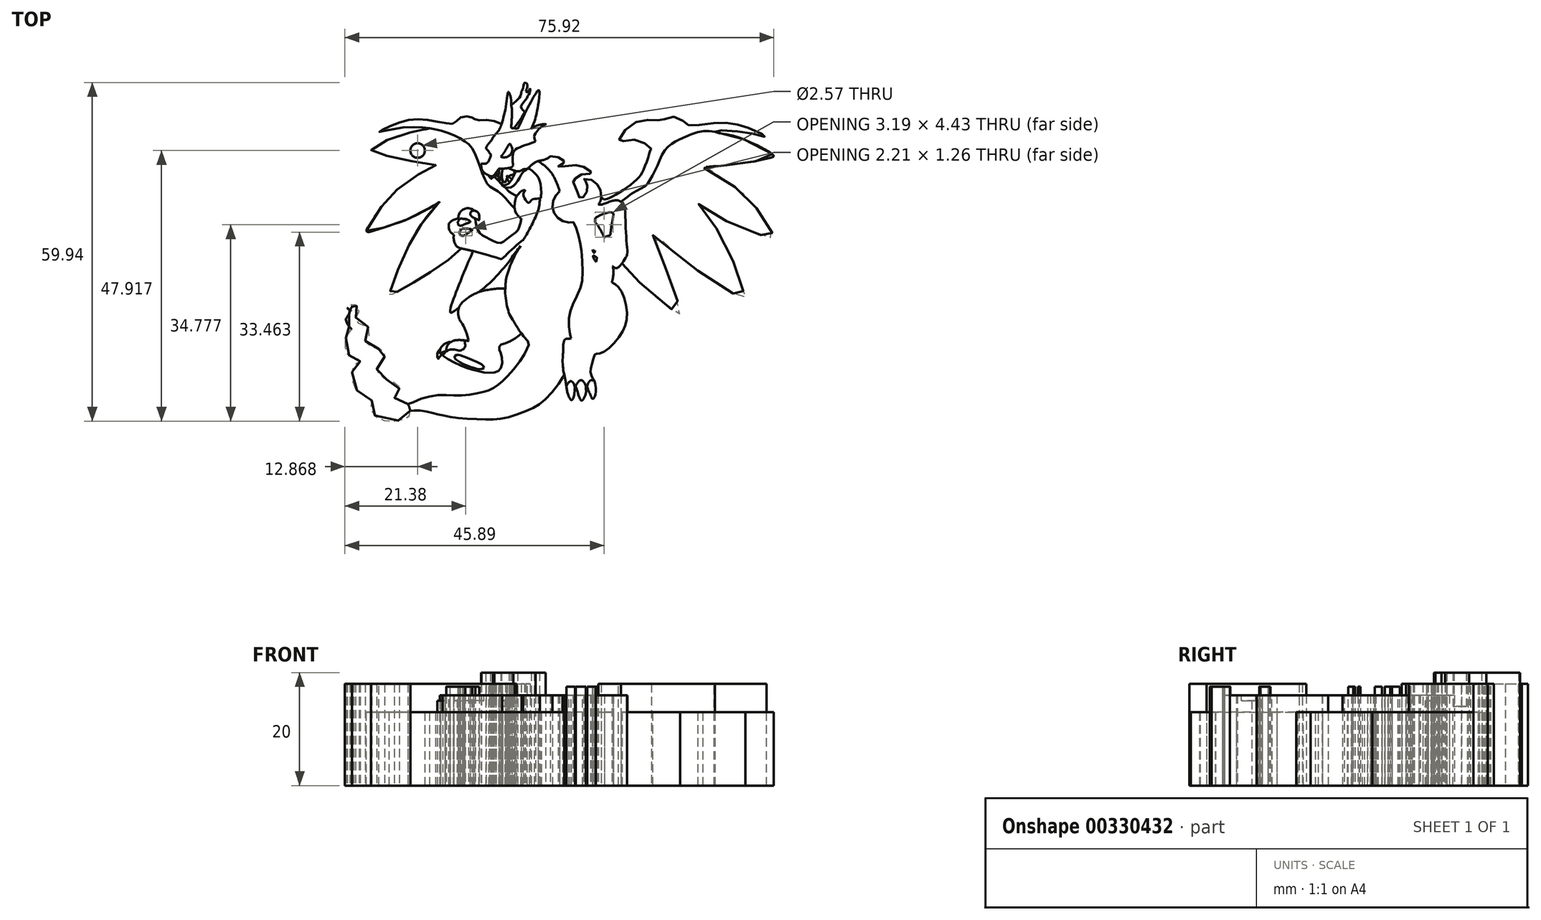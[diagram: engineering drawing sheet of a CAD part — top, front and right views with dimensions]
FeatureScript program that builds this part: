
annotation { "Feature Type Name" : "Feature", "Feature Type Description" : "" }
export const myFeature = defineFeature(function(context is Context, id is Id, definition is map)
    precondition{}
    {
        {
            var Q0;
            Q0=qCreatedBy(makeId("Top.planeOp"),FACE);
            var sketch = newSketch(context, id + "F0", { "sketchPlane" : qUnion([Q0])});
            skFitSpline(sketch, "E0", {"points": [v(-5.28, 21.77) * mm, v(-4.35, 23.75) * mm, v(-3.93, 25.14) * mm, v(-3.6, 26.95) * mm, v(-3.43, 29.56) * mm, v(-7.38, 22.36) * mm], "startDerivative": vector(5.95, 11.84) * mm, "endDerivative": vector(-15.93, -33.46) * mm});
            skFitSpline(sketch, "E1", {"points": [v(-13.6, 15.69) * mm, v(-13.11, 14.98) * mm, v(-12.33, 14.52) * mm, v(-11.58, 14.4) * mm, v(-10.53, 15.69) * mm, v(-10.29, 15.69) * mm, v(-8.86, 15.81) * mm, v(-8.3, 15.96) * mm, v(-7.97, 16.3) * mm], "startDerivative": vector(3.2, -6) * mm, "endDerivative": vector(3.22, 4.12) * mm});
            skFitSpline(sketch, "E2", {"points": [v(-7.97, 16.3) * mm, v(-8.08, 16.94) * mm, v(-8.08, 17.85) * mm, v(-7.65, 19.02) * mm, v(-4.05, 20.54) * mm, v(-3.37, 21.36) * mm, v(-2.92, 22.7) * mm, v(0.36, 24.41) * mm, v(1.08, 25) * mm, v(1.01, 25.22) * mm, v(0.6, 25.6) * mm, v(4.78, 27.86) * mm, v(5.06, 28.34) * mm, v(5.67, 28.87) * mm, v(6.78, 30.14) * mm, v(7.14, 30.28) * mm, v(7.3, 30.62) * mm, v(7.32, 30.06) * mm, v(6.76, 29.65) * mm, v(6.72, 29.1) * mm, v(6.58, 28.8) * mm, v(6.39, 28.52) * mm, v(6.25, 28.42) * mm, v(6.13, 28.24) * mm, v(6.03, 28.04) * mm, v(6, 27.9) * mm, v(6.19, 27.88) * mm, v(6.4, 28.02) * mm, v(6.72, 28.24) * mm, v(6.88, 28.28) * mm, v(6.88, 28.16) * mm, v(6.7, 27.82) * mm, v(5.89, 27.13) * mm, v(5.65, 26.9) * mm, v(5.2, 26.53) * mm, v(4.84, 26.26) * mm, v(3.81, 25.68) * mm, v(3.71, 24.24) * mm, v(3.7, 24.22) * mm, v(2.8, 23.29) * mm, v(0.4, 21.79) * mm, v(-0.37, 20.97) * mm, v(-0.98, 18.57) * mm, v(-2.38, 17.33) * mm, v(-4.18, 16.8) * mm, v(-5.54, 15.69) * mm, v(-6.16, 15.61) * mm, v(-6.94, 15.24) * mm, v(-8.86, 15.81) * mm], "startDerivative": vector(-6.92, 33.48) * mm, "endDerivative": vector(-66.57, 30.7) * mm});
            skFitSpline(sketch, "E3", {"points": [v(-13.68, 16.59) * mm, v(-13.88, 16.97) * mm, v(-13.91, 17.58) * mm, v(-13.68, 18.49) * mm, v(-12.75, 19.2) * mm], "startDerivative": vector(-1.25, 1.88) * mm, "endDerivative": vector(3.52, 2.03) * mm});
            skFitSpline(sketch, "E4", {"points": [v(-7.84, 22.85) * mm, v(-6.1, 25.41) * mm, v(-6.05, 25.88) * mm, v(-6.4, 26.2) * mm, v(-6.58, 26.84) * mm, v(-5.75, 27.92) * mm, v(-5.4, 28.63) * mm, v(-5.03, 29.25) * mm, v(-4.96, 29.82) * mm, v(-5.02, 29.88) * mm, v(-5.28, 29.43) * mm, v(-5.6, 29.25) * mm, v(-5.72, 29.44) * mm], "startDerivative": vector(12.32, 16.66) * mm, "endDerivative": vector(-1.84, 5.18) * mm});
            skFitSpline(sketch, "E5", {"points": [v(-8.36, 26.94) * mm, v(-6.68, 28.63) * mm, v(-6.54, 29.36) * mm, v(-6.31, 29.73) * mm, v(-6, 30.9) * mm, v(-5.6, 30.79) * mm, v(-5.48, 30.17) * mm, v(-5.68, 29.67) * mm, v(-5.72, 29.44) * mm], "startDerivative": vector(12.02, 9.65) * mm, "endDerivative": vector(-0.19, -3.77) * mm});
            skFitSpline(sketch, "E6", {"points": [v(-18.52, 3.96) * mm, v(-18.52, 3.16) * mm, v(-18.03, 1.98) * mm, v(-16.6, 1.46) * mm, v(-10.77, -0.1) * mm, v(-10.08, -0.26) * mm, v(-8.86, 0.8) * mm, v(-6.22, 3.05) * mm, v(-7.4, 0.84) * mm, v(-9.32, -4.35) * mm, v(-9.39, -5.44) * mm, v(-9.9, -5.49) * mm, v(-13.17, -5.89) * mm, v(-15.75, -6.98) * mm, v(-17.55, -8.73) * mm, v(-17.7, -10.16) * mm, v(-17.38, -11.25) * mm, v(-16.9, -11.96) * mm, v(-15.92, -14.74) * mm, v(-16.19, -14.77) * mm, v(-18.52, -14.74) * mm, v(-19.2, -15.08) * mm, v(-19.2, -15) * mm, v(-20.22, -15.37) * mm, v(-20.76, -15.95) * mm, v(-20.99, -16.28) * mm, v(-21.34, -16.8) * mm, v(-21.38, -17.79) * mm, v(-21.22, -17.93) * mm, v(-21.1, -17.72) * mm, v(-20.5, -17.23) * mm, v(-20.41, -17.34) * mm, v(-18.45, -18.61) * mm, v(-15.46, -19.8) * mm, v(-12.83, -20.4) * mm, v(-10.93, -20.29) * mm, v(-10.08, -19.37) * mm, v(-10.08, -17.3) * mm, v(-10.48, -16.23) * mm, v(-10.3, -15.57) * mm, v(-9.43, -15.22) * mm, v(-7.19, -14.06) * mm, v(-6.5, -13.48) * mm, v(-6.42, -13.68) * mm, v(-5.24, -15.05) * mm, v(-5.35, -15.8) * mm, v(-6.3, -17.62) * mm, v(-9.2, -21.27) * mm, v(-10.67, -22.6) * mm, v(-12.14, -23.46) * mm, v(-13.8, -23.94) * mm, v(-16.9, -24.43) * mm, v(-20.14, -24.36) * mm, v(-24.01, -24.93) * mm, v(-26.62, -25.94) * mm, v(-26.97, -25.8) * mm, v(-28.86, -25.04) * mm, v(-29.03, -24.8) * mm, v(-29.01, -24.57) * mm, v(-28.4, -23.96) * mm, v(-28.17, -23.14) * mm, v(-28.53, -22.45) * mm, v(-30.2, -21.74) * mm, v(-31.45, -20.92) * mm, v(-32.1, -20.01) * mm, v(-31.97, -19.38) * mm, v(-30.88, -18.04) * mm, v(-30.73, -17.39) * mm, v(-30.82, -16.86) * mm, v(-31.45, -16.3) * mm, v(-32.08, -16.17) * mm, v(-34.01, -15.35) * mm, v(-34.14, -14.66) * mm, v(-33.4, -13.56) * mm, v(-33.66, -12.37) * mm, v(-35.57, -11.55) * mm, v(-35.88, -10.75) * mm, v(-35.4, -10.01) * mm, v(-35.36, -9.13) * mm, v(-36.1, -8.37) * mm, v(-36.87, -8.29) * mm, v(-36.51, -8.52) * mm, v(-36.58, -8.69) * mm, v(-36.24, -9.05) * mm, v(-36.3, -9.42) * mm, v(-36.47, -9.57) * mm, v(-36.83, -9.09) * mm, v(-37.35, -8.98) * mm, v(-37.16, -9.17) * mm, v(-36.93, -9.6) * mm, v(-37.45, -10.61) * mm, v(-37.6, -11.13) * mm, v(-36.98, -12.33) * mm, v(-36.63, -12.74) * mm, v(-37.36, -13.61) * mm, v(-37.78, -15.51) * mm, v(-37.33, -17.11) * mm, v(-35.93, -17.85) * mm, v(-35.53, -17.9) * mm, v(-35.08, -18.41) * mm, v(-35.81, -18.85) * mm, v(-36.49, -19.88) * mm, v(-36.43, -21.68) * mm, v(-35.7, -23.48) * mm, v(-33.32, -24.94) * mm, v(-33.06, -25.2) * mm, v(-33.16, -26.3) * mm, v(-32.83, -27.52) * mm, v(-31.17, -28.81) * mm, v(-27.42, -28.69) * mm, v(-26.3, -27.93) * mm, v(-26.27, -26.94) * mm, v(-26.6, -25.97) * mm], "startDerivative": vector(-9.43, -93.41) * mm, "endDerivative": vector(-46.86, 115.32) * mm});
            skFitSpline(sketch, "E7", {"points": [v(-26.22, -27.2) * mm, v(-24.98, -27.1) * mm, v(-22.6, -27.46) * mm, v(-20.73, -27.93) * mm, v(-17.76, -28.4) * mm, v(-12.76, -28.7) * mm, v(-9.46, -28.44) * mm, v(-5, -26.86) * mm, v(-2.21, -25.04) * mm, v(0.9, -20.98) * mm, v(1.03, -20.68) * mm, v(1.41, -22.76) * mm, v(1.62, -23.95) * mm, v(2.3, -25.26) * mm, v(2.75, -24.57) * mm, v(2.96, -23.12) * mm, v(3.1, -22.97) * mm, v(3.43, -23.95) * mm, v(4.03, -25.29) * mm, v(4.26, -25.29) * mm, v(4.89, -23.9) * mm, v(4.92, -23) * mm, v(5.13, -23) * mm, v(5.28, -23.46) * mm, v(5.79, -24.57) * mm, v(6.08, -25.04) * mm, v(6.59, -24.16) * mm, v(6.35, -21.82) * mm, v(6.02, -21.3) * mm, v(5.7, -20.3) * mm, v(5.93, -19.03) * mm, v(6.54, -17.08) * mm, v(6.85, -17.07) * mm, v(8.28, -16.6) * mm, v(11.15, -13.47) * mm, v(12.15, -10.13) * mm, v(11.12, -5.93) * mm, v(9.82, -4.6) * mm, v(8.78, -4.2) * mm, v(7.78, -4.26) * mm], "startDerivative": vector(49.4, 7.29) * mm, "endDerivative": vector(-49.28, -7.9) * mm});
            skFitSpline(sketch, "E8", {"points": [v(9.47, -4.4) * mm, v(9.6, -3.94) * mm, v(9.59, -1.55) * mm, v(9.09, -0.86) * mm, v(9.84, -0.18) * mm, v(9.93, -0.58) * mm], "startDerivative": vector(0.87, 2.22) * mm, "endDerivative": vector(-0.3, -4.39) * mm});
            skFitSpline(sketch, "E9", {"points": [v(9.09, -0.86) * mm, v(8.73, -1.05) * mm, v(8.28, -1.45) * mm, v(7.43, -1.52) * mm, v(6.75, -0.86) * mm, v(6.18, 0) * mm, v(6.26, 0.34) * mm, v(6.82, 0) * mm, v(6.99, 0.32) * mm, v(7.62, 0.44) * mm, v(8.02, 1.4) * mm, v(7.84, 1.71) * mm, v(6.94, 1.14) * mm, v(5.95, 1.5) * mm, v(6.42, 2.81) * mm, v(9.09, 3.9) * mm, v(9.27, 4.38) * mm, v(9.73, 7.37) * mm, v(9.73, 7.79) * mm, v(9.35, 7.99) * mm, v(8.22, 7.79) * mm, v(6.57, 6.9) * mm, v(6.51, 6.18) * mm, v(5.36, 5.35) * mm], "startDerivative": vector(-12.67, -5.04) * mm, "endDerivative": vector(-28.77, -14.22) * mm});
            skFitSpline(sketch, "E10", {"points": [v(6.51, 6.18) * mm, v(7.06, 5.53) * mm, v(8.14, 3.56) * mm], "startDerivative": vector(1.37, -1.44) * mm, "endDerivative": vector(1.84, -3.64) * mm});
            skFitSpline(sketch, "E11", {"points": [v(9.59, -1.55) * mm, v(9.97, -1.83) * mm, v(10.53, -1.82) * mm, v(11.52, -0.69) * mm, v(12.14, 0.37) * mm, v(12.15, 1.95) * mm, v(11.89, 6.52) * mm, v(11.73, 8.76) * mm, v(11.1, 9.85) * mm, v(9.59, 10.03) * mm, v(7.55, 9.33) * mm, v(6.51, 9.73) * mm], "startDerivative": vector(6.81, -6.46) * mm, "endDerivative": vector(-12.01, 8.1) * mm});
            skFitSpline(sketch, "E12", {"points": [v(7.1, 9.4) * mm, v(7.47, 10.03) * mm, v(7.59, 11.2) * mm, v(7.35, 12.23) * mm, v(6.67, 13.14) * mm, v(5.54, 13.83) * mm, v(4.47, 13.8) * mm, v(4.55, 13.64) * mm, v(4.8, 13.58) * mm, v(5.07, 13.1) * mm, v(5.1, 12.27) * mm, v(4.93, 11.35) * mm, v(4.31, 10.6) * mm, v(4, 10.64) * mm, v(3.62, 10.64) * mm, v(3.52, 11.04) * mm, v(2.6, 13.52) * mm, v(2.75, 13.75) * mm, v(3.34, 14.23) * mm, v(4.77, 14.83) * mm, v(5.95, 14.83) * mm, v(5.74, 15.2) * mm, v(4.31, 16.11) * mm, v(2.7, 16.33) * mm, v(0.2, 16.04) * mm, v(0, 16.1) * mm, v(0.7, 16.57) * mm, v(1.18, 16.79) * mm, v(0.94, 17.15) * mm, v(0, 17.72) * mm, v(-1.4, 17.94) * mm], "startDerivative": vector(13.3, 18.15) * mm, "endDerivative": vector(-34.01, 2.55) * mm});
            skFitSpline(sketch, "E13", {"points": [v(7.58, 10.65) * mm, v(8.05, 10.28) * mm, v(8.35, 10.28) * mm, v(9.37, 10.7) * mm, v(11.83, 12.15) * mm, v(14.05, 13.94) * mm, v(14.85, 15.05) * mm, v(15.92, 17.75) * mm, v(16.46, 19.2) * mm, v(16.82, 18.26) * mm], "startDerivative": vector(6.95, -6.7) * mm, "endDerivative": vector(3.86, -15.3) * mm});
            skFitSpline(sketch, "E14", {"points": [v(16.46, 19.2) * mm, v(15.75, 19.97) * mm, v(13.94, 20.68) * mm, v(12.57, 20.85) * mm, v(10.74, 20.43) * mm, v(10.7, 20.63) * mm, v(11.4, 21.99) * mm, v(13.4, 23.78) * mm, v(15.64, 24.32) * mm, v(17.07, 24.38) * mm, v(18.53, 24.14) * mm, v(18.8, 24.46) * mm, v(20.22, 24.9) * mm, v(21.7, 24.44) * mm, v(22.5, 23.62) * mm, v(23.38, 23.36) * mm, v(25.33, 23.48) * mm, v(28.47, 23.81) * mm, v(30.56, 23.72) * mm, v(32.54, 23.25) * mm, v(34.73, 22.46) * mm, v(36.87, 21.31) * mm, v(36.3, 21.42) * mm, v(33.44, 22.08) * mm, v(30.02, 22.41) * mm, v(27.63, 22.38) * mm, v(27.71, 22.24) * mm, v(30.4, 21.64) * mm, v(33.06, 20.8) * mm, v(36.43, 19.2) * mm, v(38.04, 18.15) * mm, v(38.13, 17.9) * mm, v(37.8, 17.72) * mm, v(35.49, 17.15) * mm, v(32.97, 16.73) * mm, v(30.98, 16.48) * mm, v(28.54, 16.21) * mm, v(25.65, 15.93) * mm, v(25.96, 15.77) * mm, v(29.44, 13.79) * mm, v(32.6, 11.39) * mm, v(34.36, 9.6) * mm, v(35.95, 7.52) * mm, v(37.41, 5.11) * mm, v(38.14, 3.72) * mm, v(38.07, 3.42) * mm, v(37.84, 3.42) * mm, v(37, 3.58) * mm, v(31.95, 5.54) * mm, v(29.64, 6.47) * mm, v(27.1, 7.85) * mm, v(24.73, 9.48) * mm, v(25.11, 8.97) * mm, v(28.03, 5.04) * mm, v(30.2, 0.87) * mm, v(31.4, -1.72) * mm, v(32.22, -4.55) * mm, v(33.12, -7.11) * mm, v(33.05, -7.48) * mm, v(32.16, -7.11) * mm, v(28.12, -4.64) * mm, v(23.9, -1.83) * mm, v(21.26, 0.25) * mm, v(18.65, 2.66) * mm, v(16.9, 4.31) * mm, v(16.76, 4.12) * mm, v(17.68, 1.31) * mm, v(19.4, -3.07) * mm, v(20.66, -6.58) * mm, v(21.4, -8.69) * mm, v(21.47, -10.01) * mm, v(20.84, -9.75) * mm, v(16.72, -6.57) * mm, v(13.66, -3.72) * mm, v(12.07, -2.06) * mm, v(11.26, -1.06) * mm], "startDerivative": vector(-56.85, 85.17) * mm, "endDerivative": vector(-70.1, 90.18) * mm});
            skFitSpline(sketch, "E15", {"points": [v(6.51, 1.12) * mm, v(6.33, 0.84) * mm, v(6.1, 1.14) * mm, v(6.08, 1.33) * mm], "startDerivative": vector(-0.45, -1.21) * mm, "endDerivative": vector(0.05, 0.58) * mm});
            skFitSpline(sketch, "E16", {"points": [v(-15.16, 1.12) * mm, v(-15.35, 0.55) * mm, v(-15.72, -0.28) * mm, v(-16.1, -1.16) * mm, v(-16.64, -2.5) * mm, v(-17.37, -4.27) * mm, v(-17.94, -5.77) * mm, v(-18.4, -6.92) * mm, v(-18.8, -8) * mm, v(-19.03, -8.73) * mm, v(-19.12, -9.4) * mm, v(-19.12, -9.76) * mm, v(-18.88, -9.76) * mm, v(-18.22, -9.33) * mm, v(-17.62, -8.89) * mm], "startDerivative": vector(-2.72, -9.22) * mm, "endDerivative": vector(8.77, 6.5) * mm});
            skFitSpline(sketch, "E17", {"points": [v(-14.15, -6.17) * mm, v(-11.67, -4.07) * mm, v(-10.11, -2.34) * mm, v(-8.84, -0.87) * mm, v(-7.97, 0.37) * mm, v(-7.3, 1.22) * mm, v(-6.71, 2.02) * mm], "startDerivative": vector(11.76, 9.33) * mm, "endDerivative": vector(4.67, 6.46) * mm});
            skFitSpline(sketch, "E18", {"points": [v(-9.39, -5.44) * mm, v(-9.39, -6.53) * mm, v(-9.06, -8.73) * mm, v(-8.6, -10.13) * mm, v(-7.76, -11.58) * mm, v(-6.79, -13.13) * mm, v(-6.5, -13.48) * mm], "startDerivative": vector(-0.3, -6.56) * mm, "endDerivative": vector(2.62, -2.91) * mm});
            skFitSpline(sketch, "E19", {"points": [v(1.03, -20.68) * mm, v(0.8, -19.35) * mm, v(0.77, -17.84) * mm, v(0.86, -16.7) * mm, v(0.87, -15.58) * mm, v(1.03, -14.73) * mm, v(1.33, -14.42) * mm, v(2.23, -14.36) * mm, v(2.13, -13.82) * mm, v(1.86, -11.89) * mm, v(2.04, -9.88) * mm, v(2.68, -8.1) * mm, v(3.86, -5.58) * mm, v(4.27, -3.83) * mm, v(4.21, -0.14) * mm, v(3.88, 2.62) * mm, v(3.3, 4.77) * mm, v(2.73, 6.2) * mm, v(2.5, 6.2) * mm, v(1.44, 6.24) * mm, v(0.3, 6.7) * mm, v(-0.56, 7.55) * mm, v(-1, 8.66) * mm, v(-0.91, 10.02) * mm, v(-0.4, 11.1) * mm, v(0.49, 11.79) * mm, v(1.03, 11.79) * mm, v(0.7, 11.54) * mm, v(0.64, 10.9) * mm, v(1.03, 10.13) * mm, v(1.86, 9.26) * mm, v(2.59, 8.94) * mm], "startDerivative": vector(-7.7, 38.6) * mm, "endDerivative": vector(27.89, -8.8) * mm});
            skFitSpline(sketch, "E20", {"points": [v(-9.39, 12.38) * mm, v(-8.82, 11.73) * mm, v(-7.4, 10.84) * mm], "startDerivative": vector(1.21, -1.3) * mm, "endDerivative": vector(2.66, -1.76) * mm});
            skFitSpline(sketch, "E21", {"points": [v(-7.72, 8.63) * mm, v(-8.63, 9.66) * mm, v(-10, 11.14) * mm, v(-11.7, 12.3) * mm, v(-12.6, 13.07) * mm, v(-13.73, 15.6) * mm, v(-14.27, 17.1) * mm, v(-15.35, 19.45) * mm, v(-16.9, 20.76) * mm, v(-19.91, 22.17) * mm, v(-22.82, 22.85) * mm, v(-24.49, 23.03) * mm, v(-27.98, 22.94) * mm, v(-31.75, 22.22) * mm, v(-31.2, 22.54) * mm, v(-28.6, 23.73) * mm, v(-25.85, 24.4) * mm, v(-22.99, 24.28) * mm, v(-20.07, 23.8) * mm, v(-18.78, 23.64) * mm, v(-18.03, 24.12) * mm, v(-17.34, 24.76) * mm, v(-16.26, 25) * mm, v(-15.35, 24.79) * mm, v(-14.9, 24.62) * mm, v(-14.62, 24.3) * mm, v(-13.6, 24.34) * mm, v(-11.68, 24.2) * mm, v(-10.23, 23.72) * mm], "startDerivative": vector(-27.94, 30.98) * mm, "endDerivative": vector(41.35, -15.8) * mm});
            skFitSpline(sketch, "E22", {"points": [v(-17.2, 1.59) * mm, v(-17.77, 0.96) * mm, v(-19.3, -0.3) * mm, v(-20.73, -1.37) * mm, v(-23.15, -2.9) * mm, v(-24.73, -3.88) * mm, v(-26.37, -4.89) * mm, v(-27.82, -5.68) * mm, v(-29.25, -6.48) * mm, v(-29.73, -6.64) * mm, v(-29.92, -6.53) * mm, v(-29.4, -5.17) * mm, v(-28.58, -2.78) * mm, v(-27.38, 0.24) * mm, v(-25.56, 3.74) * mm, v(-24.27, 5.86) * mm, v(-22.52, 8.15) * mm, v(-20.98, 9.85) * mm, v(-21.67, 9.43) * mm, v(-24.36, 7.89) * mm, v(-27.1, 6.58) * mm, v(-29.36, 5.82) * mm, v(-33.24, 4.55) * mm, v(-33.8, 4.5) * mm, v(-33.97, 4.7) * mm, v(-32, 8.03) * mm, v(-30.12, 10.38) * mm, v(-28.05, 12.45) * mm, v(-25.06, 14.5) * mm, v(-23.24, 15.56) * mm, v(-21.7, 16.33) * mm, v(-22.7, 16.48) * mm, v(-27.8, 17.41) * mm, v(-30.28, 17.96) * mm, v(-31.88, 18.4) * mm, v(-33.1, 18.91) * mm, v(-33.05, 19.1) * mm, v(-31.87, 19.96) * mm, v(-28.99, 21.35) * mm, v(-26.32, 22.11) * mm, v(-23.53, 22.68) * mm, v(-22.82, 22.85) * mm], "startDerivative": vector(-29.61, -35.9) * mm, "endDerivative": vector(38.43, 10.72) * mm});
            skFitSpline(sketch, "E23", {"points": [v(5.13, -23) * mm, v(5.2, -22.5) * mm, v(5.45, -21.99) * mm, v(5.78, -21.74) * mm, v(6.04, -21.76) * mm, v(6.35, -21.82) * mm], "startDerivative": vector(0.13, 2.24) * mm, "endDerivative": vector(1.8, -0.38) * mm});
            skFitSpline(sketch, "E24", {"points": [v(4.92, -23) * mm, v(4.79, -22.5) * mm, v(4.43, -21.97) * mm, v(4.13, -21.73) * mm, v(3.77, -21.82) * mm, v(3.3, -22.32) * mm, v(3.14, -22.56) * mm, v(3.1, -22.97) * mm], "startDerivative": vector(-0.56, 3.28) * mm, "endDerivative": vector(0.05, -3.42) * mm});
            skFitSpline(sketch, "E25", {"points": [v(2.96, -23.12) * mm, v(2.87, -22.8) * mm, v(2.73, -22.38) * mm, v(2.38, -21.96) * mm, v(2.17, -21.91) * mm, v(1.73, -22.27) * mm, v(1.41, -22.76) * mm], "startDerivative": vector(-0.62, 2.2) * mm, "endDerivative": vector(-1.38, -2.6) * mm});
            skFitSpline(sketch, "E26", {"points": [v(2.23, -14.36) * mm, v(2.47, -15) * mm, v(3.12, -15.77) * mm, v(3.68, -16.2) * mm], "startDerivative": vector(0.5, -2.05) * mm, "endDerivative": vector(1.74, -1.18) * mm});
            skFitSpline(sketch, "E27", {"points": [v(-20.5, -17.23) * mm, v(-20.16, -17) * mm, v(-20.05, -16.8) * mm, v(-20.11, -16.67) * mm, v(-20.7, -16.96) * mm, v(-20.9, -17.06) * mm, v(-20.95, -16.64) * mm, v(-20.87, -16.1) * mm], "startDerivative": vector(2.5, 1.5) * mm, "endDerivative": vector(0.62, 2.8) * mm});
            skFitSpline(sketch, "E28", {"points": [v(-19.2, -15.08) * mm, v(-19.64, -15.6) * mm, v(-19.85, -16.3) * mm, v(-19.84, -16.61) * mm, v(-19.77, -16.62) * mm, v(-19.61, -16.53) * mm, v(-19.35, -16.4) * mm, v(-18.89, -16.3) * mm, v(-18.21, -16.36) * mm, v(-17.57, -16.5) * mm, v(-17.1, -16.39) * mm, v(-16.75, -16.2) * mm, v(-16.5, -15.79) * mm, v(-16.48, -15.4) * mm, v(-16.6, -14.88) * mm, v(-16.6, -14.7) * mm], "startDerivative": vector(-5.8, -5.41) * mm, "endDerivative": vector(0.07, 3.46) * mm});
            skFitSpline(sketch, "E29", {"points": [v(-17.86, 6.89) * mm, v(-16.95, 6.84) * mm, v(-16.35, 6.77) * mm, v(-15.85, 6.56) * mm, v(-15.6, 6.36) * mm, v(-15.63, 6.24) * mm, v(-15.82, 6.13) * mm, v(-16.39, 5.96) * mm, v(-16.78, 5.78) * mm, v(-16.93, 5.62) * mm, v(-17.13, 5.3) * mm], "startDerivative": vector(6.2, 0.23) * mm, "endDerivative": vector(-2.2, -3.51) * mm});
            skFitSpline(sketch, "E30", {"points": [v(-17.37, 6.87) * mm, v(-17.58, 6.64) * mm, v(-17.77, 6.33) * mm, v(-17.77, 5.97) * mm, v(-17.69, 5.74) * mm, v(-17.42, 5.62) * mm, v(-17.12, 5.63) * mm, v(-16.93, 5.62) * mm], "startDerivative": vector(-1.47, -1.23) * mm, "endDerivative": vector(1.5, -0.25) * mm});
            skFitSpline(sketch, "E31", {"points": [v(-15.67, 6.45) * mm, v(-14.72, 6.71) * mm], "startDerivative": vector(0.93, 0.26) * mm, "endDerivative": vector(0.93, 0.26) * mm});
            skFitSpline(sketch, "E32", {"points": [v(-6.22, 3.05) * mm, v(-5.63, 4.06) * mm, v(-4.78, 5.62) * mm, v(-3.9, 7.5) * mm, v(-3.4, 8.9) * mm, v(-3.28, 10.46) * mm], "startDerivative": vector(3.33, 5.57) * mm, "endDerivative": vector(0.22, 7.72) * mm});
            skFitSpline(sketch, "E33", {"points": [v(-3.56, 17.04) * mm, v(-2.28, 16.1) * mm, v(-1.2, 14.93) * mm, v(-0.28, 13.18) * mm, v(0.23, 11.68) * mm], "startDerivative": vector(5.45, -3.75) * mm, "endDerivative": vector(1.8, -6) * mm});
            skFitSpline(sketch, "E34", {"points": [v(27.71, 22.24) * mm, v(24.96, 22.24) * mm, v(21.71, 20.96) * mm, v(19.97, 20.06) * mm, v(18.62, 18.6) * mm, v(17.5, 16.21) * mm, v(16.38, 13.95) * mm, v(15.48, 12.71) * mm, v(13.8, 11.79) * mm, v(11.1, 9.85) * mm], "startDerivative": vector(-22.42, 2.58) * mm, "endDerivative": vector(-21.3, -16.83) * mm});
            skLineSegment(sketch, "E35", {"start": v(-10.01, 13.1) * mm, "end": v(-10, 13.1) * mm});
            skFitSpline(sketch, "E36", {"points": [v(-9.89, 15.69) * mm, v(-10, 15) * mm, v(-10.08, 14.61) * mm, v(-10.18, 14.06) * mm, v(-10.23, 13.83) * mm], "startDerivative": vector(-0.44, -2.42) * mm, "endDerivative": vector(-0.2, -1.12) * mm});
            skFitSpline(sketch, "E37", {"points": [v(-10, 15) * mm, v(-10, 14.25) * mm, v(-9.88, 13.68) * mm, v(-9.66, 13.36) * mm, v(-9.39, 13.33) * mm, v(-9.22, 13.54) * mm, v(-9.14, 13.95) * mm, v(-9.05, 14.09) * mm, v(-9.11, 14.39) * mm, v(-8.2, 13.83) * mm], "startDerivative": vector(-0.21, -5.26) * mm, "endDerivative": vector(7.45, -5.58) * mm});
            skFitSpline(sketch, "E38", {"points": [v(-8.63, 13.3) * mm, v(-8.77, 13.42) * mm, v(-8.96, 13.72) * mm, v(-9.05, 14.09) * mm], "startDerivative": vector(-0.52, 0.4) * mm, "endDerivative": vector(-0.16, 0.99) * mm});
            skFitSpline(sketch, "E39", {"points": [v(-8.85, 14.29) * mm, v(-8.52, 14.51) * mm, v(-8.13, 14.61) * mm, v(-7.82, 14.84) * mm, v(-7.75, 15) * mm, v(-7.77, 15.36) * mm], "startDerivative": vector(1.41, 1.24) * mm, "endDerivative": vector(-0.25, 1.92) * mm});
            skFitSpline(sketch, "E40", {"points": [v(-10.34, 17.82) * mm, v(-10.08, 17.94) * mm, v(-8.6, 20.26) * mm], "startDerivative": vector(0.94, 0.18) * mm, "endDerivative": vector(2.3, 4.03) * mm});
            skFitSpline(sketch, "E41", {"points": [v(-8.7, 20.06) * mm, v(-8.55, 20.07) * mm, v(-8.42, 19.88) * mm, v(-8.2, 19.41) * mm, v(-8.16, 18.97) * mm, v(-8.26, 18.6) * mm, v(-8.45, 18.24) * mm, v(-8.7, 17.98) * mm, v(-9.02, 17.8) * mm, v(-9.5, 17.7) * mm, v(-9.98, 17.74) * mm, v(-10.2, 17.86) * mm], "startDerivative": vector(2.88, 0.72) * mm, "endDerivative": vector(-2.61, 1.71) * mm});
            skFitSpline(sketch, "E42", {"points": [v(-9.3, 19.03) * mm, v(-9.12, 18.93) * mm, v(-9, 18.62) * mm, v(-8.94, 18.22) * mm, v(-8.94, 17.83) * mm], "startDerivative": vector(1, -0.31) * mm, "endDerivative": vector(-0.07, -1.41) * mm});
            skFitSpline(sketch, "E43", {"points": [v(-9.54, 18.66) * mm, v(-9.43, 18.52) * mm, v(-9.38, 18.16) * mm, v(-9.44, 17.99) * mm, v(-9.52, 17.93) * mm, v(-9.66, 18.02) * mm, v(-9.76, 18.1) * mm, v(-9.81, 18.26) * mm], "startDerivative": vector(0.87, -0.76) * mm, "endDerivative": vector(-0.23, 1.4) * mm});
            skFitSpline(sketch, "E44", {"points": [v(-13.19, -19.54) * mm, v(-13.27, -19.2) * mm, v(-16.25, -17.74) * mm, v(-17.57, -17.27) * mm, v(-18.01, -17.27) * mm, v(-18.37, -17.62) * mm, v(-18.04, -18.12) * mm, v(-17.2, -18.69) * mm, v(-16.18, -19.16) * mm, v(-15.04, -19.55) * mm, v(-13.8, -19.77) * mm, v(-13.19, -19.54) * mm]});
            skFitSpline(sketch, "E45", {"points": [v(-10.53, 15.69) * mm, v(-10.53, 14.99) * mm, v(-10.58, 14.57) * mm, v(-10.68, 14.3) * mm, v(-10.74, 14.3) * mm, v(-10.82, 14.47) * mm, v(-10.93, 14.87) * mm, v(-11, 15.06) * mm], "startDerivative": vector(0.07, -3.4) * mm, "endDerivative": vector(-0.45, 1.46) * mm});
            skFitSpline(sketch, "E46", {"points": [v(-12.24, 14.48) * mm, v(-12.26, 14.34) * mm, v(-12.1, 14.15) * mm, v(-11.91, 13.95) * mm, v(-11.8, 13.96) * mm, v(-11.8, 14.14) * mm, v(-11.85, 14.34) * mm], "startDerivative": vector(-0.38, -0.96) * mm, "endDerivative": vector(-0.25, 1.1) * mm});
            skFitSpline(sketch, "E47", {"points": [v(-11.1, 14.9) * mm, v(-11.04, 14.75) * mm, v(-11.03, 14.5) * mm, v(-11.04, 14.42) * mm, v(-11.2, 14.44) * mm, v(-11.29, 14.46) * mm, v(-11.36, 14.6) * mm], "startDerivative": vector(0.45, -0.79) * mm, "endDerivative": vector(-0.4, 0.95) * mm});
            skFitSpline(sketch, "E48", {"points": [v(-11.83, 14.27) * mm, v(-11.69, 14.13) * mm, v(-11.56, 14.15) * mm, v(-11.58, 14.4) * mm], "startDerivative": vector(0.38, -0.54) * mm, "endDerivative": vector(-0.22, 0.81) * mm});
            skFitSpline(sketch, "E49", {"points": [v(-11.57, 14.41) * mm, v(-11.48, 14.25) * mm, v(-11.4, 14.2) * mm, v(-11.35, 14.24) * mm, v(-11.35, 14.47) * mm, v(-11.37, 14.58) * mm], "startDerivative": vector(0.34, -0.74) * mm, "endDerivative": vector(-0.14, 0.47) * mm});
            skFitSpline(sketch, "E50", {"points": [v(-4.05, 20.54) * mm, v(-4.05, 20.54) * mm], "startDerivative": vector(0, 0) * mm, "endDerivative": vector(0, 0) * mm});
            skFitSpline(sketch, "E51", {"points": [v(-16.74, 3.84) * mm, v(-17.03, 3.84) * mm, v(-17.34, 3.95) * mm, v(-17.52, 4.36) * mm, v(-17.29, 4.82) * mm, v(-16.97, 5.1) * mm], "startDerivative": vector(-1.69, -0.22) * mm, "endDerivative": vector(1.72, 0.62) * mm});
            skFitSpline(sketch, "E52", {"points": [v(-14.72, 6.9) * mm, v(-14.83, 6.96) * mm, v(-15.18, 7.12) * mm, v(-15.44, 7.36) * mm, v(-15.6, 7.65) * mm, v(-15.52, 7.98) * mm, v(-15.3, 8.18) * mm, v(-15.07, 8.28) * mm], "startDerivative": vector(-0.65, 1.56) * mm, "endDerivative": vector(1.92, -0.34) * mm});
            skLineSegment(sketch, "E53", {"start": v(-26.22, -27.2) * mm, "end": v(-26.22, -27.2) * mm});
            skFitSpline(sketch, "E54", {"points": [v(-26.6, -25.97) * mm, v(-26.62, -25.94) * mm], "startDerivative": vector(0, 0.03) * mm, "endDerivative": vector(0, 0.03) * mm});
            skFitSpline(sketch, "E55", {"points": [v(-20.11, -16.67) * mm, v(-19.94, -16.57) * mm, v(-19.84, -16.61) * mm], "startDerivative": vector(0.32, 0.25) * mm, "endDerivative": vector(0.23, -0.14) * mm});
            skFitSpline(sketch, "E56", {"points": [v(-4.93, 22.46) * mm, v(-5.28, 21.77) * mm], "startDerivative": vector(-0.34, -0.68) * mm, "endDerivative": vector(-0.34, -0.68) * mm});
            skLineSegment(sketch, "E57", {"start": v(-7.19, 22.77) * mm, "end": v(-7.19, 22.77) * mm});
            skFitSpline(sketch, "E58", {"points": [v(-8.52, 22.85) * mm, v(-8.52, 22.85) * mm], "startDerivative": vector(0, 0) * mm, "endDerivative": vector(0, 0) * mm});
            skFitSpline(sketch, "E59", {"points": [v(-7.5, 15.28) * mm, v(-7.65, 14.94) * mm, v(-7.91, 14.43) * mm, v(-8.2, 13.83) * mm, v(-8.63, 13.3) * mm, v(-8.92, 13.02) * mm, v(-9.3, 12.83) * mm, v(-9.7, 12.8) * mm, v(-10.08, 13.03) * mm], "startDerivative": vector(-1.2, -3.03) * mm, "endDerivative": vector(-3.1, 2.52) * mm});
            skFitSpline(sketch, "E60", {"points": [v(-4.05, 20.54) * mm, v(-4.23, 20.98) * mm, v(-4.22, 21.56) * mm, v(-3.9, 22.18) * mm, v(-3.48, 22.68) * mm, v(-3.07, 23.08) * mm, v(-2.63, 23.36) * mm, v(-2.32, 23.53) * mm, v(-2.22, 23.6) * mm, v(-2.64, 23.58) * mm, v(-3.32, 23.47) * mm, v(-4.05, 23.23) * mm, v(-4.52, 22.9) * mm, v(-4.79, 22.76) * mm], "startDerivative": vector(-2.85, 5.53) * mm, "endDerivative": vector(-4.35, -1.8) * mm});
            skFitSpline(sketch, "E61", {"points": [v(-7.19, 22.77) * mm, v(-7.84, 22.85) * mm, v(-8.36, 22.94) * mm, v(-8.36, 23.1) * mm, v(-8.26, 24.3) * mm, v(-8.22, 26.35) * mm, v(-8.36, 26.94) * mm, v(-8.36, 27.81) * mm, v(-8.65, 28.95) * mm, v(-8.85, 29.3) * mm, v(-9.1, 28.35) * mm, v(-9.42, 26.05) * mm, v(-9.9, 24.08) * mm, v(-10.07, 23.6) * mm, v(-10.23, 23.72) * mm], "startDerivative": vector(-9.9, 1.4) * mm, "endDerivative": vector(-4.88, 5.53) * mm});
            skFitSpline(sketch, "E62", {"points": [v(-13.6, 15.69) * mm, v(-13.68, 16.59) * mm], "startDerivative": vector(-0.08, 0.9) * mm, "endDerivative": vector(-0.08, 0.9) * mm});
            skFitSpline(sketch, "E63", {"points": [v(-13.68, 16.59) * mm, v(-13.11, 16.59) * mm, v(-12.66, 16.7) * mm, v(-12.1, 17.54) * mm, v(-11.97, 18.23) * mm, v(-12.15, 18.44) * mm, v(-12.54, 19.03) * mm, v(-12.75, 19.2) * mm, v(-12.66, 19.75) * mm, v(-11.86, 20.74) * mm, v(-11.37, 21.51) * mm, v(-10.64, 22.33) * mm, v(-10.07, 23.5) * mm], "startDerivative": vector(7.89, -0.1) * mm, "endDerivative": vector(4.3, 11.2) * mm});
            skFitSpline(sketch, "E64", {"points": [v(-10.07, 23.5) * mm, v(-10.07, 23.6) * mm], "startDerivative": vector(0, 0.1) * mm, "endDerivative": vector(0, 0.1) * mm});
            skFitSpline(sketch, "E65", {"points": [v(-10.23, 23.72) * mm, v(-10.49, 23.6) * mm, v(-10.96, 23.02) * mm, v(-11.18, 22.46) * mm, v(-11.18, 22.08) * mm, v(-11.06, 21.86) * mm], "startDerivative": vector(-1.53, -0.4) * mm, "endDerivative": vector(0.95, -1.33) * mm});
            skFitSpline(sketch, "E66", {"points": [v(-11.34, 14.3) * mm, v(-10.34, 13.26) * mm], "startDerivative": vector(1, -1.05) * mm, "endDerivative": vector(1, -1.05) * mm});
            skFitSpline(sketch, "E67", {"points": [v(-10.08, 13.03) * mm, v(-10.17, 13.1) * mm], "startDerivative": vector(-0.09, 0.08) * mm, "endDerivative": vector(-0.09, 0.08) * mm});
            skFitSpline(sketch, "E68", {"points": [v(-10.23, 23.72) * mm, v(-10.23, 23.72) * mm], "startDerivative": vector(0, 0) * mm, "endDerivative": vector(0, 0) * mm});
            skFitSpline(sketch, "E69", {"points": [v(6.82, 0) * mm, v(6.75, -0.61) * mm, v(6.73, -0.83) * mm], "startDerivative": vector(-0.12, -1.1) * mm, "endDerivative": vector(-0.06, -0.52) * mm});
            skFitSpline(sketch, "E70", {"points": [v(-10, 15) * mm, v(-10, 15) * mm], "startDerivative": vector(0, 0) * mm, "endDerivative": vector(0, 0) * mm});
            skFitSpline(sketch, "E71", {"points": [v(-5.6, 15.58) * mm, v(-5.54, 15.69) * mm], "startDerivative": vector(0.06, 0.11) * mm, "endDerivative": vector(0.06, 0.11) * mm});
            skCircle(sketch, "E72", {"center": v(-24.91, 18.92) * mm, "radius": 1.28 * mm});
            skFitSpline(sketch, "E73", {"points": [v(-10.01, 12.97) * mm, v(-10, 12.8) * mm, v(-9.63, 12.5) * mm, v(-9.39, 12.38) * mm, v(-8.42, 12.38) * mm, v(-7.54, 13.04) * mm, v(-6.71, 14.31) * mm, v(-6.3, 15.05) * mm, v(-5.71, 15.47) * mm, v(-5.21, 15.7) * mm, v(-4.35, 15.1) * mm, v(-3.62, 14.23) * mm, v(-3.13, 12.93) * mm, v(-3.05, 10.9) * mm, v(-3.11, 10.53) * mm, v(-3.28, 10.46) * mm], "startDerivative": vector(-1.07, -5.29) * mm, "endDerivative": vector(-5.8, -1.47) * mm});
            skFitSpline(sketch, "E74", {"points": [v(-3.28, 10.46) * mm, v(-3.96, 10.37) * mm, v(-4.7, 10.18) * mm, v(-5.25, 9.63) * mm, v(-5.6, 9.9) * mm, v(-6, 10.56) * mm, v(-6.17, 11.2) * mm, v(-6.02, 11.67) * mm, v(-5.88, 11.83) * mm, v(-6.3, 11.84) * mm, v(-7.18, 11.09) * mm, v(-7.4, 10.84) * mm], "startDerivative": vector(-6.74, -0.99) * mm, "endDerivative": vector(-2.57, -2.9) * mm});
            skFitSpline(sketch, "E75", {"points": [v(-7.4, 10.84) * mm, v(-7.61, 10.17) * mm, v(-7.75, 9.26) * mm, v(-7.72, 8.63) * mm, v(-7.53, 7.95) * mm, v(-7.05, 7.28) * mm, v(-6.6, 6.9) * mm, v(-6.54, 6.86) * mm, v(-6.94, 5.32) * mm, v(-7.35, 4.63) * mm, v(-9.18, 3.2) * mm, v(-10.28, 2.56) * mm, v(-11.48, 2.92) * mm, v(-12.99, 3.66) * mm, v(-14.1, 4.56) * mm, v(-14.55, 5.9) * mm, v(-14.72, 6.71) * mm, v(-14.72, 6.9) * mm, v(-14.55, 6.85) * mm, v(-14.22, 6.63) * mm, v(-14.04, 6.6) * mm, v(-14, 6.98) * mm, v(-14.06, 7.65) * mm, v(-14.5, 8.18) * mm, v(-14.93, 8.27) * mm, v(-15.07, 8.28) * mm], "startDerivative": vector(-5.59, -15.7) * mm, "endDerivative": vector(-6.52, 0.47) * mm});
            skFitSpline(sketch, "E76", {"points": [v(-10.17, 13.1) * mm, v(-10.34, 13.26) * mm, v(-10.45, 13.61) * mm, v(-10.5, 14.03) * mm, v(-10.48, 14.22) * mm, v(-10.26, 13.9) * mm, v(-10.23, 13.83) * mm, v(-9.94, 13.59) * mm, v(-9.93, 13.18) * mm, v(-10.17, 13.1) * mm]});
            skFitSpline(sketch, "E77", {"points": [v(-18.52, 3.96) * mm, v(-18.13, 4.63) * mm, v(-17.38, 5.04) * mm, v(-16.97, 5.1) * mm, v(-15.77, 5.05) * mm, v(-15.25, 4.86) * mm, v(-15.56, 4.58) * mm, v(-16.33, 4.1) * mm, v(-16.74, 3.84) * mm], "startDerivative": vector(2.11, 5.32) * mm, "endDerivative": vector(-3.49, -2.26) * mm});
            skFitSpline(sketch, "E78", {"points": [v(-18.49, 4.04) * mm, v(-18.91, 4.3) * mm, v(-19.33, 4.98) * mm, v(-19.35, 5.93) * mm, v(-18.85, 6.47) * mm, v(-17.86, 6.89) * mm], "startDerivative": vector(-2.76, 1.36) * mm, "endDerivative": vector(4.57, 1.63) * mm});
            skFitSpline(sketch, "E79", {"points": [v(-17.7, 6.89) * mm, v(-17.62, 7.6) * mm, v(-16.97, 8.39) * mm, v(-16.13, 8.69) * mm, v(-15.25, 8.53) * mm, v(-14.86, 8.26) * mm], "startDerivative": vector(-0.15, 3.7) * mm, "endDerivative": vector(2.16, -1.81) * mm});
            skSolve(sketch);
        }
        {
            var Q0;
            {var subQ14=sQuery(id+"F0.wireOp",EDGE,"E18");Q0=makeQuery(id+"F0.imprint","IMPRINT",FACE,{"disambiguationData":[TD([[makeQuery(id+"F0.imprint","IMPRINT",EDGE,{"derivedFrom":subQ14}),1.0]])]});}
            var Q1;
            {var subQ6=sQuery(id+"F0.wireOp",EDGE,"E22");Q1=makeQuery(id+"F0.imprint","IMPRINT",FACE,{"disambiguationData":[TD([[makeQuery(id+"F0.imprint","IMPRINT",EDGE,{"derivedFrom":subQ6}),-1.0]])]});}
            var Q2;
            {var subQ3=sQuery(id+"F0.wireOp",EDGE,"E34");Q2=makeQuery(id+"F0.imprint","IMPRINT",FACE,{"disambiguationData":[TD([[makeQuery(id+"F0.imprint","IMPRINT",EDGE,{"derivedFrom":subQ3}),1.0]])]});}
            var Q3;
            {var subQ0=sQuery(id+"F0.wireOp",EDGE,"E16");Q3=makeQuery(id+"F0.imprint","IMPRINT",FACE,{"disambiguationData":[TD([[makeQuery(id+"F0.imprint","IMPRINT",EDGE,{"derivedFrom":subQ0}),1.0]])]});}
            var Q4;
            {var subQ0=sQuery(id+"F0.wireOp",EDGE,"E10");Q4=makeQuery(id+"F0.imprint","IMPRINT",FACE,{"disambiguationData":[TD([[makeQuery(id+"F0.imprint","IMPRINT",EDGE,{"derivedFrom":subQ0}),1.0]])]});}
            extrude(context, id + "F1", {"entities" : qUnion([Q0, Q1, Q2, Q3, Q4]), "depth" : 13 * mm, "offsetDistance" : 25 * mm});
        }
        {
            var Q0;
            {var subQ19=sQuery(id+"F0.wireOp",EDGE,"E10");Q0=makeQuery(id+"F0.imprint","IMPRINT",FACE,{"disambiguationData":[TD([[makeQuery(id+"F0.imprint","IMPRINT",EDGE,{"derivedFrom":subQ19}),-1.0]])]});}
            var Q1;
            {var subQ3=sQuery(id+"F0.wireOp",EDGE,"E30");Q1=makeQuery(id+"F0.imprint","IMPRINT",FACE,{"disambiguationData":[TD([[makeQuery(id+"F0.imprint","IMPRINT",EDGE,{"derivedFrom":subQ3}),-1.0]])]});}
            var Q2;
            {var subQ4=sQuery(id+"F0.wireOp",EDGE,"E18");Q2=makeQuery(id+"F0.imprint","IMPRINT",FACE,{"disambiguationData":[TD([[makeQuery(id+"F0.imprint","IMPRINT",EDGE,{"derivedFrom":subQ4}),-1.0]])]});}
            var Q3;
            {var subQ0=sQuery(id+"F0.wireOp",EDGE,"E31");Q3=makeQuery(id+"F0.imprint","IMPRINT",FACE,{"disambiguationData":[TD([[makeQuery(id+"F0.imprint","IMPRINT",EDGE,{"derivedFrom":subQ0}),1.0]])]});}
            extrude(context, id + "F2", {"entities" : qUnion([Q0, Q1, Q2, Q3]), "depth" : 16 * mm, "offsetDistance" : 25 * mm});
        }
        {
            var Q0;
            {var subQ9=sQuery(id+"F0.wireOp",EDGE,"E3");Q0=makeQuery(id+"F0.imprint","IMPRINT",FACE,{"disambiguationData":[TD([[makeQuery(id+"F0.imprint","IMPRINT",EDGE,{"derivedFrom":subQ9}),1.0]])]});}
            var Q1;
            {var subQ3=sQuery(id+"F0.wireOp",EDGE,"E34");Q1=makeQuery(id+"F0.imprint","IMPRINT",FACE,{"disambiguationData":[TD([[makeQuery(id+"F0.imprint","IMPRINT",EDGE,{"derivedFrom":subQ3}),-1.0]])]});}
            var Q2;
            {var subQ2=sQuery(id+"F0.wireOp",EDGE,"E54");Q2=makeQuery(id+"F0.imprint","IMPRINT",FACE,{"disambiguationData":[TD([[makeQuery(id+"F0.imprint","IMPRINT",EDGE,{"derivedFrom":subQ2}),1.0]])]});}
            var Q3;
            {var subQ0=sQuery(id+"F0.wireOp",EDGE,"E4");Q3=makeQuery(id+"F0.imprint","IMPRINT",FACE,{"disambiguationData":[TD([[makeQuery(id+"F0.imprint","IMPRINT",EDGE,{"derivedFrom":subQ0}),1.0]])]});}
            var Q4;
            {var subQ3=sQuery(id+"F0.wireOp",EDGE,"E50");Q4=makeQuery(id+"F0.imprint","IMPRINT",FACE,{"disambiguationData":[TD([[makeQuery(id+"F0.imprint","IMPRINT",EDGE,{"derivedFrom":subQ3}),-1.0]])]});}
            var Q5;
            {var subQ0=sQuery(id+"F0.wireOp",EDGE,"E3");Q5=makeQuery(id+"F0.imprint","IMPRINT",FACE,{"disambiguationData":[TD([[makeQuery(id+"F0.imprint","IMPRINT",EDGE,{"derivedFrom":subQ0}),-1.0]])]});}
            var Q6;
            {var subQ2=sQuery(id+"F0.wireOp",EDGE,"E64");Q6=makeQuery(id+"F0.imprint","IMPRINT",FACE,{"disambiguationData":[TD([[makeQuery(id+"F0.imprint","IMPRINT",EDGE,{"derivedFrom":subQ2}),1.0]])]});}
            extrude(context, id + "F3", {"entities" : qUnion([Q0, Q1, Q2, Q3, Q4, Q5, Q6]), "depth" : 18 * mm, "offsetDistance" : 25 * mm});
        }
        {
            var Q0;
            {var subQ0=sQuery(id+"F0.wireOp",EDGE,"E30");Q0=makeQuery(id+"F0.imprint","IMPRINT",FACE,{"disambiguationData":[TD([[makeQuery(id+"F0.imprint","IMPRINT",EDGE,{"derivedFrom":subQ0}),1.0]])]});}
            var Q1;
            {var subQ0=sQuery(id+"F0.wireOp",EDGE,"E52");Q1=makeQuery(id+"F0.imprint","IMPRINT",FACE,{"disambiguationData":[TD([[makeQuery(id+"F0.imprint","IMPRINT",EDGE,{"derivedFrom":subQ0}),-1.0]])]});}
            var Q2;
            {var subQ0=sQuery(id+"F0.wireOp",EDGE,"E51");Q2=makeQuery(id+"F0.imprint","IMPRINT",FACE,{"disambiguationData":[TD([[makeQuery(id+"F0.imprint","IMPRINT",EDGE,{"derivedFrom":subQ0}),-1.0]])]});}
            var Q3;
            {var subQ0=sQuery(id+"F0.wireOp",EDGE,"E69");Q3=makeQuery(id+"F0.imprint","IMPRINT",FACE,{"disambiguationData":[TD([[makeQuery(id+"F0.imprint","IMPRINT",EDGE,{"derivedFrom":subQ0}),-1.0]])]});}
            var Q4;
            {var subQ0=sQuery(id+"F0.wireOp",EDGE,"E15");Q4=makeQuery(id+"F0.imprint","IMPRINT",FACE,{"disambiguationData":[TD([[makeQuery(id+"F0.imprint","IMPRINT",EDGE,{"derivedFrom":subQ0}),-1.0]])]});}
            var Q5;
            {var subQ0=sQuery(id+"F0.wireOp",EDGE,"E28");var subQ1=sQuery(id+"F0.wireOp",EDGE,"E6");var subQ2=makeQuery(id+"F0.imprint","INTERSECT",VERTEX,{"disambiguationData":[OD(0.0)],"derivedFrom":[subQ1,subQ0]});Q5=makeQuery(id+"F0.imprint","IMPRINT",FACE,{"disambiguationData":[TD([[makeQuery(id+"F0.imprint","IMPRINT",EDGE,{"disambiguationData":[TD([[subQ2,1.0]])],"derivedFrom":subQ1}),1.0]])]});}
            var Q6;
            {var subQ0=sQuery(id+"F0.wireOp",EDGE,"E25");Q6=makeQuery(id+"F0.imprint","IMPRINT",FACE,{"disambiguationData":[TD([[makeQuery(id+"F0.imprint","IMPRINT",EDGE,{"derivedFrom":subQ0}),1.0]])]});}
            var Q7;
            {var subQ0=sQuery(id+"F0.wireOp",EDGE,"E24");Q7=makeQuery(id+"F0.imprint","IMPRINT",FACE,{"disambiguationData":[TD([[makeQuery(id+"F0.imprint","IMPRINT",EDGE,{"derivedFrom":subQ0}),1.0]])]});}
            var Q8;
            {var subQ0=sQuery(id+"F0.wireOp",EDGE,"E23");Q8=makeQuery(id+"F0.imprint","IMPRINT",FACE,{"disambiguationData":[TD([[makeQuery(id+"F0.imprint","IMPRINT",EDGE,{"derivedFrom":subQ0}),-1.0]])]});}
            extrude(context, id + "F4", {"entities" : qUnion([Q0, Q1, Q2, Q3, Q4, Q5, Q6, Q7, Q8]), "depth" : 17.5 * mm, "offsetDistance" : 25 * mm});
        }
        {
            var Q0;
            {var subQ3=sQuery(id+"F0.wireOp",EDGE,"E60");Q0=makeQuery(id+"F0.imprint","IMPRINT",FACE,{"disambiguationData":[TD([[makeQuery(id+"F0.imprint","IMPRINT",EDGE,{"derivedFrom":subQ3}),1.0]])]});}
            extrude(context, id + "F5", {"entities" : qUnion([Q0]), "depth" : 20 * mm, "offsetDistance" : 25 * mm});
        }
        {
            var Q0;
            {var subQ0=sQuery(id+"F0.wireOp",EDGE,"E45");Q0=makeQuery(id+"F0.imprint","IMPRINT",FACE,{"disambiguationData":[TD([[makeQuery(id+"F0.imprint","IMPRINT",EDGE,{"derivedFrom":subQ0}),-1.0]])]});}
            var Q1;
            {var subQ0=sQuery(id+"F0.wireOp",EDGE,"E47");Q1=makeQuery(id+"F0.imprint","IMPRINT",FACE,{"disambiguationData":[TD([[makeQuery(id+"F0.imprint","IMPRINT",EDGE,{"derivedFrom":subQ0}),-1.0]])]});}
            var Q2;
            {var subQ0=sQuery(id+"F0.wireOp",EDGE,"E49");var subQ1=sQuery(id+"F0.wireOp",EDGE,"E1");var subQ2=makeQuery(id+"F0.imprint","INTERSECT",VERTEX,{"disambiguationData":[OD(0.0)],"derivedFrom":[subQ1,subQ0]});Q2=makeQuery(id+"F0.imprint","IMPRINT",FACE,{"disambiguationData":[TD([[makeQuery(id+"F0.imprint","IMPRINT",EDGE,{"disambiguationData":[TD([[subQ2,-1.0]])],"derivedFrom":subQ1}),-1.0]])]});}
            var Q3;
            {var subQ3=sQuery(id+"F0.wireOp",EDGE,"E48");Q3=makeQuery(id+"F0.imprint","IMPRINT",FACE,{"disambiguationData":[TD([[makeQuery(id+"F0.imprint","IMPRINT",EDGE,{"derivedFrom":subQ3}),1.0]])]});}
            var Q4;
            {var subQ0=sQuery(id+"F0.wireOp",EDGE,"E46");var subQ1=sQuery(id+"F0.wireOp",EDGE,"E1");var subQ2=makeQuery(id+"F0.imprint","INTERSECT",VERTEX,{"disambiguationData":[OD(0.0)],"derivedFrom":[subQ1,subQ0]});Q4=makeQuery(id+"F0.imprint","IMPRINT",FACE,{"disambiguationData":[TD([[makeQuery(id+"F0.imprint","IMPRINT",EDGE,{"disambiguationData":[TD([[subQ2,-1.0]])],"derivedFrom":subQ1}),-1.0]])]});}
            var Q5;
            {var subQ0=sQuery(id+"F0.wireOp",EDGE,"E76");var subQ1=makeQuery(id+"F0.imprint","INTERSECT",VERTEX,{"derivedFrom":[sQuery(id+"F0.wireOp",EDGE,"E66"),subQ0]});Q5=makeQuery(id+"F0.imprint","IMPRINT",FACE,{"disambiguationData":[TD([[makeQuery(id+"F0.imprint","IMPRINT",EDGE,{"disambiguationData":[TD([[subQ1,1.0]])],"derivedFrom":subQ0}),-1.0]])]});}
            var Q6;
            {var subQ0=sQuery(id+"F0.wireOp",EDGE,"E38");Q6=makeQuery(id+"F0.imprint","IMPRINT",FACE,{"disambiguationData":[TD([[makeQuery(id+"F0.imprint","IMPRINT",EDGE,{"derivedFrom":subQ0}),-1.0]])]});}
            extrude(context, id + "F6", {"entities" : qUnion([Q0, Q1, Q2, Q3, Q4, Q5, Q6]), "depth" : 18 * mm, "offsetDistance" : 25 * mm});
        }
        {
            var Q0;
            {var subQ8=sQuery(id+"F0.wireOp",EDGE,"E39");Q0=makeQuery(id+"F0.imprint","IMPRINT",FACE,{"disambiguationData":[TD([[makeQuery(id+"F0.imprint","IMPRINT",EDGE,{"derivedFrom":subQ8}),1.0]])]});}
            extrude(context, id + "F7", {"entities" : qUnion([Q0]), "depth" : 16 * mm, "offsetDistance" : 25 * mm});
        }
        {
            var Q0;
            {var subQ0=sQuery(id+"F0.wireOp",EDGE,"E39");Q0=makeQuery(id+"F0.imprint","IMPRINT",FACE,{"disambiguationData":[TD([[makeQuery(id+"F0.imprint","IMPRINT",EDGE,{"derivedFrom":subQ0}),-1.0]])]});}
            var Q1;
            {var subQ1=sQuery(id+"F0.wireOp",EDGE,"E38");Q1=makeQuery(id+"F0.imprint","IMPRINT",FACE,{"disambiguationData":[TD([[makeQuery(id+"F0.imprint","IMPRINT",EDGE,{"derivedFrom":subQ1}),1.0]])]});}
            extrude(context, id + "F8", {"entities" : qUnion([Q0, Q1]), "depth" : 15 * mm, "offsetDistance" : 25 * mm});
        }
        {
            var Q0;
            {var subQ5=sQuery(id+"F0.wireOp",EDGE,"E43");Q0=makeQuery(id+"F0.imprint","IMPRINT",FACE,{"disambiguationData":[TD([[makeQuery(id+"F0.imprint","IMPRINT",EDGE,{"derivedFrom":subQ5}),1.0]])]});}
            var Q1;
            {var subQ0=sQuery(id+"F0.wireOp",EDGE,"E43");Q1=makeQuery(id+"F0.imprint","IMPRINT",FACE,{"disambiguationData":[TD([[makeQuery(id+"F0.imprint","IMPRINT",EDGE,{"derivedFrom":subQ0}),-1.0]])]});}
            extrude(context, id + "F9", {"entities" : qUnion([Q0, Q1]), "operationType" : NewBodyOperationType.ADD, "depth" : 14 * mm, "offsetDistance" : 25 * mm});
        }
        {
            var Q0;
            Q0=makeQuery(id+"F0.imprint","IMPRINT",FACE,{"disambiguationData":[TD([[makeQuery(id+"F0.imprint","IMPRINT",EDGE,{"derivedFrom":sQuery(id+"F0.wireOp",EDGE,"E44")}),1.0]])]});
            extrude(context, id + "F10", {"entities" : qUnion([Q0]), "operationType" : NewBodyOperationType.ADD, "depth" : 15 * mm, "offsetDistance" : 25 * mm});
        }
        {
            var Q0;
            {var subQ5=sQuery(id+"F0.wireOp",EDGE,"E55");Q0=makeQuery(id+"F0.imprint","IMPRINT",FACE,{"disambiguationData":[TD([[makeQuery(id+"F0.imprint","IMPRINT",EDGE,{"derivedFrom":subQ5}),1.0]])]});}
            extrude(context, id + "F11", {"entities" : qUnion([Q0]), "depth" : 16 * mm, "offsetDistance" : 25 * mm});
        }
        {
            var Q0;
            {var subQ0=sQuery(id+"F0.wireOp",EDGE,"E27");var subQ1=sQuery(id+"F0.wireOp",EDGE,"E6");var subQ2=makeQuery(id+"F0.imprint","INTERSECT",VERTEX,{"disambiguationData":[OD(0.0)],"derivedFrom":[subQ1,subQ0]});Q0=makeQuery(id+"F0.imprint","IMPRINT",FACE,{"disambiguationData":[TD([[makeQuery(id+"F0.imprint","IMPRINT",EDGE,{"disambiguationData":[TD([[subQ2,1.0]])],"derivedFrom":subQ1}),1.0]])]});}
            extrude(context, id + "F12", {"entities" : qUnion([Q0]), "depth" : 15 * mm, "offsetDistance" : 25 * mm});
        }
    });
